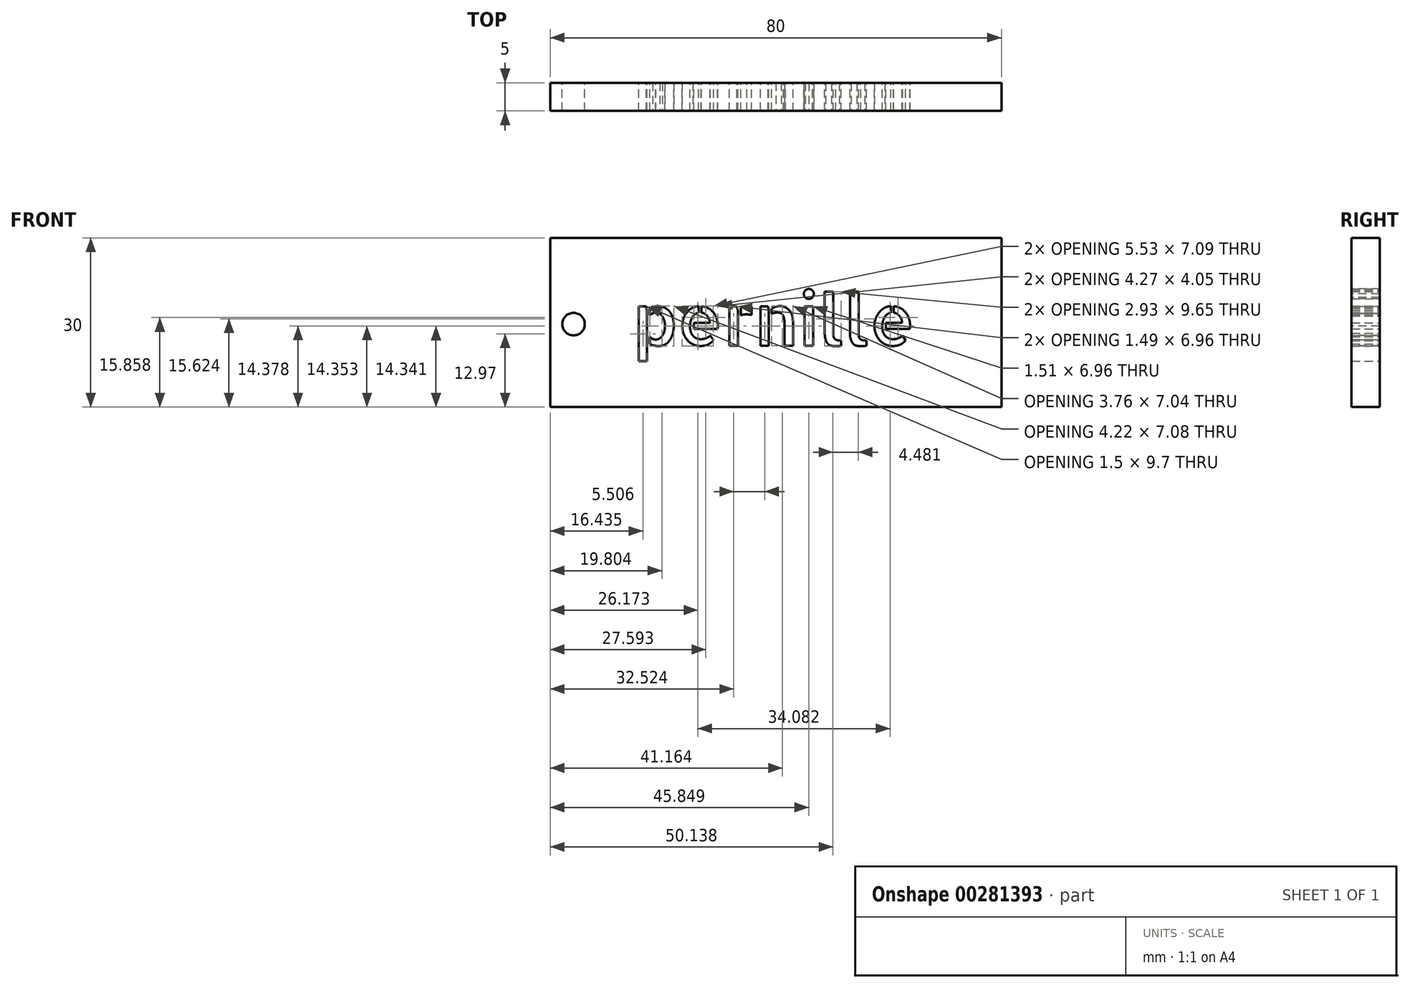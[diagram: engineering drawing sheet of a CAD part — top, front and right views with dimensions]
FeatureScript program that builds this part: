
annotation { "Feature Type Name" : "Feature", "Feature Type Description" : "" }
export const myFeature = defineFeature(function(context is Context, id is Id, definition is map)
    precondition{}
    {
        {
            var Q0;
            Q0=qCreatedBy(makeId("Front.planeOp"),FACE);
            var sketch = newSketch(context, id + "F0", { "sketchPlane" : qUnion([Q0])});
            skLineSegment(sketch, "E0.bottom", {"start": v(-30.62, 0) * mm, "end": v(49.38, 0) * mm});
            skLineSegment(sketch, "E0.top", {"start": v(-30.62, 30) * mm, "end": v(49.38, 30) * mm});
            skLineSegment(sketch, "E0.left", {"start": v(-30.62, 0) * mm, "end": v(-30.62, 30) * mm});
            skLineSegment(sketch, "E0.right", {"start": v(49.38, 0) * mm, "end": v(49.38, 30) * mm});
            skText(sketch, "E1", { "text": "pernille", "fontName": "AllertaStencil-Regular.ttf"});
            skCircle(sketch, "E2", {"center": v(-26.48, 14.7) * mm, "radius": 2 * mm});
            const initialGuessF0  = {"E1": [-0.016, 0.01086, 1, 0, 0.0091]};
            skSetInitialGuess(sketch, initialGuessF0);
            skSolve(sketch);
        }
        {
            var Q0;
            Q0 = qSketchRegion(id + "F0", true);
            extrude(context, id + "F1", {"entities" : qUnion([Q0]), "depth" : 5 * mm});
        }
    });
